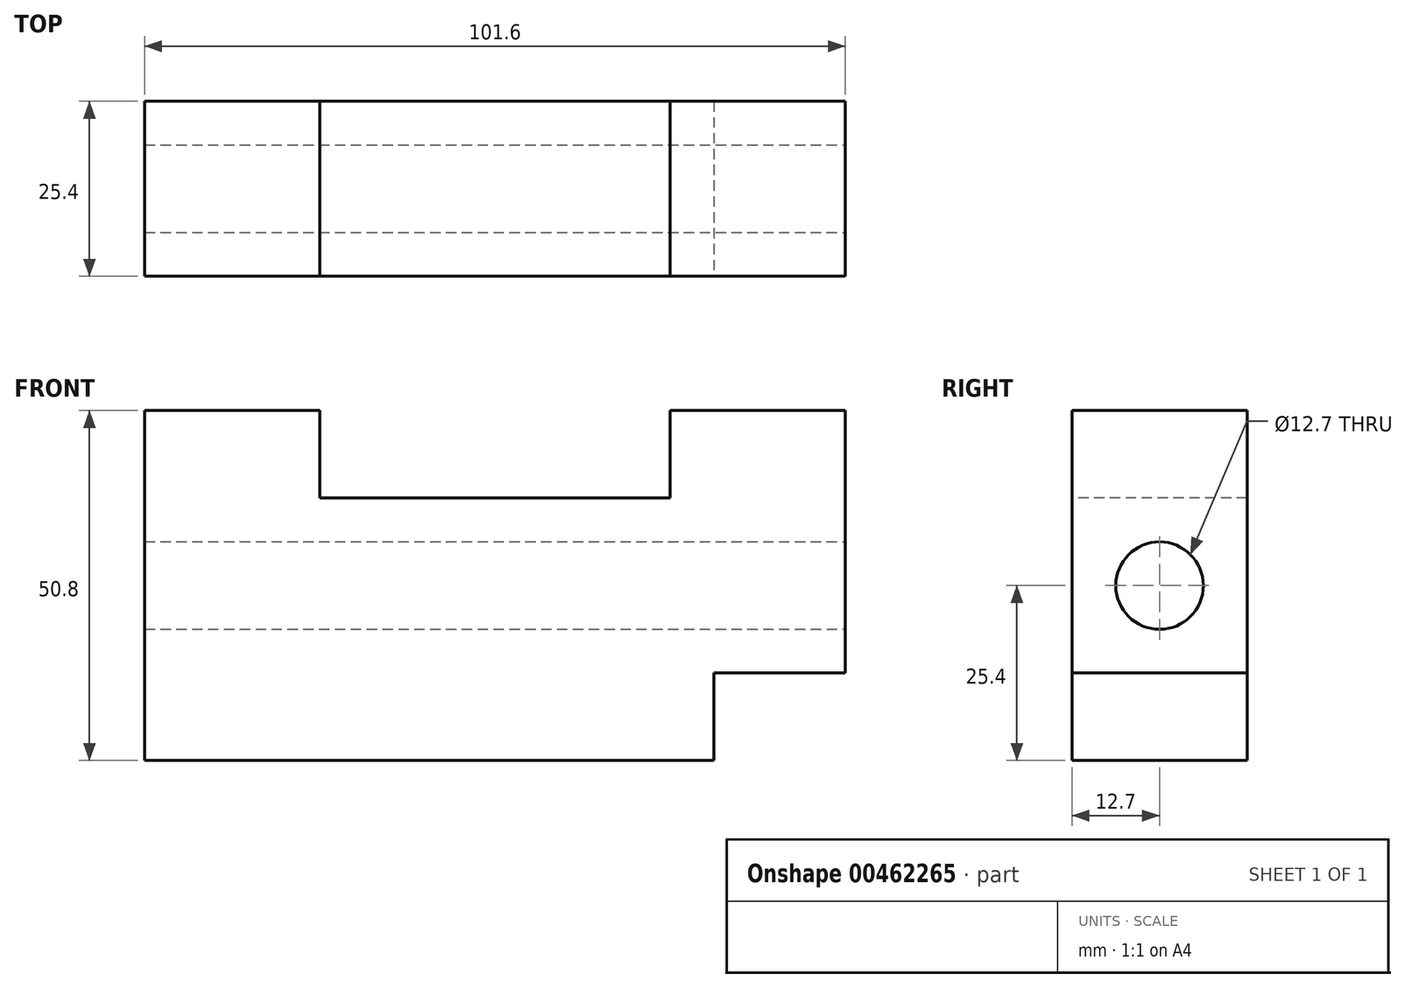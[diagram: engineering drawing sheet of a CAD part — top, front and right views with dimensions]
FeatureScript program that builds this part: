
annotation { "Feature Type Name" : "Feature", "Feature Type Description" : "" }
export const myFeature = defineFeature(function(context is Context, id is Id, definition is map)
    precondition{}
    {
        {
            var Q0;
            Q0=qCreatedBy(makeId("Front.planeOp"),FACE);
            var sketch = newSketch(context, id + "F0", { "sketchPlane" : qUnion([Q0])});
            skLineSegment(sketch, "E0.bottom", {"start": v(50.8, 25.4) * mm, "end": v(-50.8, 25.4) * mm});
            skLineSegment(sketch, "E0.top", {"start": v(50.8, -25.4) * mm, "end": v(-50.8, -25.4) * mm});
            skLineSegment(sketch, "E0.left", {"start": v(50.8, 25.4) * mm, "end": v(50.8, -25.4) * mm});
            skLineSegment(sketch, "E0.right", {"start": v(-50.8, 25.4) * mm, "end": v(-50.8, -25.4) * mm});
            skPoint(sketch, "E0.middle", {"position": v(0, 0) * mm});
            skSolve(sketch);
        }
        {
            var Q0;
            Q0=makeQuery(id+"F0.imprint","IMPRINT",FACE,{"disambiguationData":[TD([[makeQuery(id+"F0.imprint","IMPRINT",EDGE,{"derivedFrom":sQuery(id+"F0.wireOp",EDGE,"E0.bottom")}),1.0]])]});
            extrude(context, id + "F1", {"entities" : qUnion([Q0]), "depth" : 25.4 * mm});
        }
        {
            var Q0;
            Q0=makeQuery(id+"F1.opExtrude","CAP_FACE",FACE,{"disambiguationData":[OSD([sQuery(id+"F0.wireOp",EDGE,"E0.bottom"),sQuery(id+"F0.wireOp",EDGE,"E0.top"),sQuery(id+"F0.wireOp",EDGE,"E0.left"),sQuery(id+"F0.wireOp",EDGE,"E0.right")])],"isStart":false});
            var sketch = newSketch(context, id + "F2", { "sketchPlane" : qUnion([Q0])});
            skLineSegment(sketch, "E1.bottom", {"start": v(-25.4, 25.4) * mm, "end": v(25.4, 25.4) * mm});
            skLineSegment(sketch, "E1.top", {"start": v(-25.4, 12.7) * mm, "end": v(25.4, 12.7) * mm});
            skLineSegment(sketch, "E1.left", {"start": v(-25.4, 25.4) * mm, "end": v(-25.4, 12.7) * mm});
            skLineSegment(sketch, "E1.right", {"start": v(25.4, 25.4) * mm, "end": v(25.4, 12.7) * mm});
            skSolve(sketch);
        }
        {
            var Q0;
            Q0=makeQuery(id+"F2.imprint","IMPRINT",FACE,{"disambiguationData":[TD([[makeQuery(id+"F2.imprint","IMPRINT",EDGE,{"derivedFrom":sQuery(id+"F2.wireOp",EDGE,"E1.bottom")}),1.0]])]});
            extrude(context, id + "F3", {"entities" : qUnion([Q0]), "operationType" : NewBodyOperationType.REMOVE, "endBound" : BoundingType.THROUGH_ALL, "oppositeDirection" : true, "depth" : 25.4 * mm});
        }
        {
            var Q0;
            Q0=makeQuery(id+"F1.opExtrude","CAP_FACE",FACE,{"disambiguationData":[OSD([sQuery(id+"F0.wireOp",EDGE,"E0.bottom"),sQuery(id+"F0.wireOp",EDGE,"E0.top"),sQuery(id+"F0.wireOp",EDGE,"E0.left"),sQuery(id+"F0.wireOp",EDGE,"E0.right")])],"isStart":false});
            var sketch = newSketch(context, id + "F4", { "sketchPlane" : qUnion([Q0])});
            skLineSegment(sketch, "E2.bottom", {"start": v(31.75, -25.4) * mm, "end": v(50.8, -25.4) * mm});
            skLineSegment(sketch, "E2.top", {"start": v(31.75, -12.7) * mm, "end": v(50.8, -12.7) * mm});
            skLineSegment(sketch, "E2.left", {"start": v(31.75, -25.4) * mm, "end": v(31.75, -12.7) * mm});
            skLineSegment(sketch, "E2.right", {"start": v(50.8, -25.4) * mm, "end": v(50.8, -12.7) * mm});
            skSolve(sketch);
        }
        {
            var Q0;
            Q0=makeQuery(id+"F4.imprint","IMPRINT",FACE,{"disambiguationData":[TD([[makeQuery(id+"F4.imprint","IMPRINT",EDGE,{"derivedFrom":sQuery(id+"F4.wireOp",EDGE,"E2.bottom")}),-1.0]])]});
            extrude(context, id + "F5", {"entities" : qUnion([Q0]), "operationType" : NewBodyOperationType.REMOVE, "endBound" : BoundingType.THROUGH_ALL, "oppositeDirection" : true, "depth" : 25.4 * mm});
        }
        {
            var Q0;
            Q0=qCreatedBy(makeId("Right.planeOp"),FACE);
            var sketch = newSketch(context, id + "F6", { "sketchPlane" : qUnion([Q0])});
            skCircle(sketch, "E3", {"center": v(-12.7, 0) * mm, "radius": 6.35 * mm});
            skSolve(sketch);
        }
        {
            var Q0;
            Q0 = qSketchRegion(id + "F6", true);
            extrude(context, id + "F7", {"entities" : qUnion([Q0]), "operationType" : NewBodyOperationType.ADD, "endBound" : BoundingType.THROUGH_ALL, "depth" : 25.4 * mm});
        }
        {
            var Q0;
            Q0=makeQuery(id+"F7.opExtrude","CAP_FACE",FACE,{"disambiguationData":[OSD([sQuery(id+"F6.wireOp",EDGE,"E3")])],"isStart":false});
            extrude(context, id + "F8", {"entities" : qUnion([Q0]), "operationType" : NewBodyOperationType.REMOVE, "endBound" : BoundingType.THROUGH_ALL, "oppositeDirection" : true, "depth" : 25.4 * mm});
        }
    });
